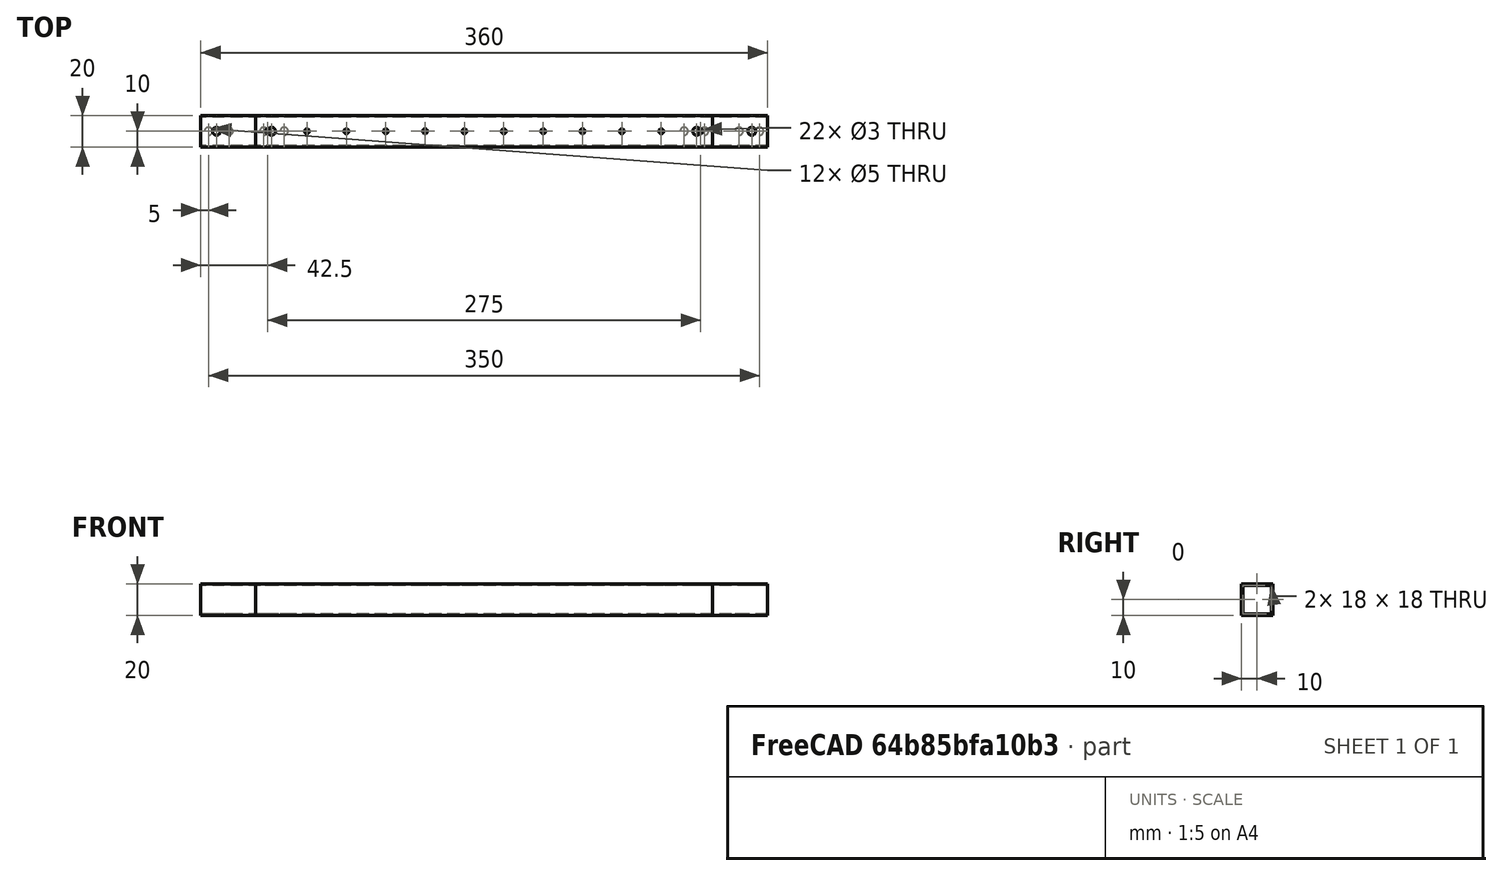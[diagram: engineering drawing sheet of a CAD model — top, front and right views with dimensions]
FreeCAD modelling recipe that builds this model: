
FCSTD DOCUMENT  (FreeCAD 0.19R24291 (Git))
Label: carbon-fiber-tube
License: Other
LicenseURL: GPL3
objects: TechDraw::DrawViewDimension×15, Sketcher::SketchObject×12, PartDesign::Pocket×10, TechDraw::DrawViewPart×6, TechDraw::DrawViewBalloon×6, PartDesign::LinearPattern×4, PartDesign::Pad×2, PartDesign::Body×2, TechDraw::DrawSVGTemplate×2, TechDraw::DrawViewAnnotation×2, TechDraw::DrawPage×2
note: 42 computed .brp shape members not serialized (recipe doc carries the construction recipe); baked Part::Feature solids carry a one-line shape summary decoded from their .brp

FEATURE [Sketcher::SketchObject] Sketch
  FullyConstrained = true
  MapMode = 5
  Support = -> [XY_Plane]
  sketch-geometry (4):
    g0: LineSegment StartX=-145 StartY=10 StartZ=0 EndX=145 EndY=10 EndZ=0
    g1: LineSegment StartX=145 StartY=10 StartZ=0 EndX=145 EndY=-10 EndZ=0
    g2: LineSegment StartX=145 StartY=-10 StartZ=0 EndX=-145 EndY=-10 EndZ=0
    g3: LineSegment StartX=-145 StartY=-10 StartZ=0 EndX=-145 EndY=10 EndZ=0
  constraints (12):
    c: Coincident(g0,g1)
    c: Coincident(g1,g2)
    c: Coincident(g2,g3)
    c: Coincident(g3,g0)
    c: Horizontal(g0)
    c: Horizontal(g2)
    c: Vertical(g1)
    c: Vertical(g3)
    c: DistanceX(g0,g0) = 290
    c: DistanceX(g0,g-1) = 145
    c: DistanceY(g3,g3) = 20
    c: DistanceY(g2,g-1) = 10
FEATURE [PartDesign::Pad] Pad
  Direction = (1,1,1)
  Length = 20
  Length2 = 100
  Profile = -> Sketch
  Type = 0
FEATURE [Sketcher::SketchObject] Sketch001
  FullyConstrained = true
  MapMode = 5
  Placement = pos=(145,0,0) rot=(0.57735,0.57735,0.57735;2.0944rad)
  Support = -> [Pad]
  sketch-geometry (4):
    g0: LineSegment StartX=-9 StartY=19 StartZ=0 EndX=9 EndY=19 EndZ=0
    g1: LineSegment StartX=9 StartY=19 StartZ=0 EndX=9 EndY=1 EndZ=0
    g2: LineSegment StartX=9 StartY=1 StartZ=0 EndX=-9 EndY=1 EndZ=0
    g3: LineSegment StartX=-9 StartY=1 StartZ=0 EndX=-9 EndY=19 EndZ=0
  constraints (12):
    c: Coincident(g0,g1)
    c: Coincident(g1,g2)
    c: Coincident(g2,g3)
    c: Coincident(g3,g0)
    c: Horizontal(g0)
    c: Horizontal(g2)
    c: Vertical(g1)
    c: Vertical(g3)
    c: DistanceX(g0,g0) = 18
    c: DistanceX(g2,g-1) = 9
    c: DistanceY(g3,g3) = 18
    c: DistanceY(g-1,g2) = 1
FEATURE [PartDesign::Pocket] Pocket
  BaseFeature = -> Pad
  Length = 5
  Length2 = 100
  Profile = -> Sketch001
  Type = 1
FEATURE [Sketcher::SketchObject] Sketch002
  FullyConstrained = true
  MapMode = 5
  Placement = pos=(0,0,20) rot=(0,0,1;0rad)
  Support = -> [Pocket]
  sketch-geometry (6):
    g0: LineSegment StartX=-145 StartY=10 StartZ=0 EndX=145 EndY=10 EndZ=0
    g1: LineSegment StartX=145 StartY=10 StartZ=0 EndX=145 EndY=-10 EndZ=0
    g2: LineSegment StartX=145 StartY=-10 StartZ=0 EndX=-145 EndY=-10 EndZ=0
    g3: LineSegment StartX=-145 StartY=-10 StartZ=0 EndX=-145 EndY=10 EndZ=0
    g4: Circle CenterX=-135 CenterY=0 CenterZ=0 NormalX=0 NormalY=0 NormalZ=1 AngleXU=0 Radius=2.5
    g5: Circle CenterX=135 CenterY=0 CenterZ=0 NormalX=0 NormalY=0 NormalZ=1 AngleXU=0 Radius=2.5
  constraints (18):
    c: Coincident(g0,g1)
    c: Coincident(g1,g2)
    c: Coincident(g2,g3)
    c: Coincident(g3,g0)
    c: Horizontal(g0)
    c: Horizontal(g2)
    c: Vertical(g1)
    c: Vertical(g3)
    c: DistanceX(g0,g0) = 290
    c: DistanceX(g0,g-1) = 145
    c: DistanceY(g3,g3) = 20
    c: DistanceY(g2,g-1) = 10
    c: PointOnObject(g4,g-1)
    c: PointOnObject(g5,g-1)
    c: Radius(g5) = 2.5
    c: Radius(g4) = 2.5
    c: DistanceX(g5,g0) = 10
    c: DistanceX(g0,g4) = 10
FEATURE [PartDesign::Pocket] Pocket001
  BaseFeature = -> Pocket
  Length = 5
  Length2 = 100
  Profile = -> Sketch002
  Type = 0
FEATURE [Sketcher::SketchObject] Sketch003
  FullyConstrained = true
  MapMode = 5
  Placement = pos=(0,0,0) rot=(1,0,0;3.14159rad)
  Support = -> [Pocket001]
  sketch-geometry (4):
    g0: Circle CenterX=-140 CenterY=0 CenterZ=0 NormalX=0 NormalY=0 NormalZ=1 AngleXU=0 Radius=2.5
    g1: Circle CenterX=-127 CenterY=0 CenterZ=0 NormalX=0 NormalY=0 NormalZ=1 AngleXU=0 Radius=2.5
    g2: Circle CenterX=140 CenterY=0 CenterZ=0 NormalX=0 NormalY=0 NormalZ=1 AngleXU=0 Radius=2.5
    g3: Circle CenterX=127 CenterY=0 CenterZ=0 NormalX=0 NormalY=0 NormalZ=1 AngleXU=0 Radius=2.5
  constraints (12):
    c: PointOnObject(g0,g-1)
    c: PointOnObject(g1,g-1)
    c: PointOnObject(g2,g-1)
    c: PointOnObject(g3,g-1)
    c: Radius(g2) = 2.5
    c: Radius(g3) = 2.5
    c: Radius(g0) = 2.5
    c: Radius(g1) = 2.5
    c: DistanceX(g0,g-1) = 140
    c: DistanceX(g1,g-1) = 127
    c: DistanceX(g-1,g2) = 140
    c: DistanceX(g-1,g3) = 127
FEATURE [PartDesign::Pocket] Pocket002
  BaseFeature = -> Pocket001
  Length = 5
  Length2 = 100
  Profile = -> Sketch003
  Type = 0
FEATURE [Sketcher::SketchObject] Sketch004
  FullyConstrained = true
  MapMode = 5
  Placement = pos=(0,0,20) rot=(0,0,1;0rad)
  Support = -> [Pocket002]
  sketch-geometry (1):
    g0: Circle CenterX=12.5 CenterY=0 CenterZ=0 NormalX=0 NormalY=0 NormalZ=1 AngleXU=0 Radius=1.5
  constraints (3):
    c: PointOnObject(g0,g-1)
    c: Radius(g0) = 1.5
    c: DistanceX(g-1,g0) = 12.5
FEATURE [PartDesign::Pocket] Pocket003
  BaseFeature = -> Pocket002
  Length = 5
  Length2 = 100
  Profile = -> Sketch004
  Type = 0
FEATURE [PartDesign::LinearPattern] LinearPattern
  BaseFeature = -> Pocket003
  Direction = -> Sketch004 [H_Axis]
  Length = 100
  Occurrences = 5
  Originals = -> [Pocket003]
FEATURE [Sketcher::SketchObject] Sketch005
  FullyConstrained = true
  MapMode = 5
  Placement = pos=(0,0,20) rot=(0,0,1;0rad)
  Support = -> [LinearPattern]
  sketch-geometry (1):
    g0: Circle CenterX=-12.5 CenterY=0 CenterZ=0 NormalX=0 NormalY=0 NormalZ=1 AngleXU=0 Radius=1.5
  constraints (3):
    c: PointOnObject(g0,g-1)
    c: Radius(g0) = 1.5
    c: DistanceX(g0,g-1) = 12.5
FEATURE [PartDesign::Pocket] Pocket004
  BaseFeature = -> LinearPattern
  Length = 5
  Length2 = 100
  Profile = -> Sketch005
  Type = 0
FEATURE [PartDesign::LinearPattern] LinearPattern001
  BaseFeature = -> Pocket004
  Direction = -> Sketch005 [H_Axis]
  Length = 100
  Occurrences = 5
  Originals = -> [Pocket004]
  Reversed = true
FEATURE [PartDesign::Body] Body  label="180-tube"
  Group = -> [Sketch,Pad,Sketch001,Pocket,Sketch002,Pocket001,Sketch003,Pocket002,Sketch004,Pocket003,LinearPattern,Sketch005,Pocket004,LinearPattern001]
  Origin = -> Origin
  Tip = -> LinearPattern001
FEATURE [Sketcher::SketchObject] Sketch006
  FullyConstrained = true
  MapMode = 5
  Support = -> [XY_Plane001]
  sketch-geometry (4):
    g0: LineSegment StartX=-180 StartY=10 StartZ=0 EndX=180 EndY=10 EndZ=0
    g1: LineSegment StartX=180 StartY=10 StartZ=0 EndX=180 EndY=-10 EndZ=0
    g2: LineSegment StartX=180 StartY=-10 StartZ=0 EndX=-180 EndY=-10 EndZ=0
    g3: LineSegment StartX=-180 StartY=-10 StartZ=0 EndX=-180 EndY=10 EndZ=0
  constraints (12):
    c: Coincident(g0,g1)
    c: Coincident(g1,g2)
    c: Coincident(g2,g3)
    c: Coincident(g3,g0)
    c: Horizontal(g0)
    c: Horizontal(g2)
    c: Vertical(g1)
    c: Vertical(g3)
    c: DistanceY(g-1,g0) = 10
    c: DistanceY(g3,g3) = 20
    c: DistanceX(g0,g0) = 360
    c: DistanceX(g0,g-1) = 180
FEATURE [PartDesign::Pad] Pad001
  Direction = (1,1,1)
  Length = 20
  Length2 = 100
  Profile = -> Sketch006
  Type = 0
FEATURE [Sketcher::SketchObject] Sketch007
  FullyConstrained = true
  MapMode = 5
  Placement = pos=(180,0,0) rot=(0.57735,0.57735,0.57735;2.0944rad)
  Support = -> [Pad001]
  sketch-geometry (4):
    g0: LineSegment StartX=-9 StartY=19 StartZ=0 EndX=9 EndY=19 EndZ=0
    g1: LineSegment StartX=9 StartY=19 StartZ=0 EndX=9 EndY=1 EndZ=0
    g2: LineSegment StartX=9 StartY=1 StartZ=0 EndX=-9 EndY=1 EndZ=0
    g3: LineSegment StartX=-9 StartY=1 StartZ=0 EndX=-9 EndY=19 EndZ=0
  constraints (12):
    c: Coincident(g0,g1)
    c: Coincident(g1,g2)
    c: Coincident(g2,g3)
    c: Coincident(g3,g0)
    c: Horizontal(g0)
    c: Horizontal(g2)
    c: Vertical(g1)
    c: Vertical(g3)
    c: DistanceX(g0,g0) = 18
    c: DistanceX(g2,g-1) = 9
    c: DistanceY(g3,g3) = 18
    c: DistanceY(g-1,g2) = 1
FEATURE [PartDesign::Pocket] Pocket005
  BaseFeature = -> Pad001
  Length = 5
  Length2 = 100
  Profile = -> Sketch007
  Type = 1
FEATURE [Sketcher::SketchObject] Sketch008
  FullyConstrained = true
  MapMode = 5
  Placement = pos=(0,0,20) rot=(0,0,1;0rad)
  Support = -> [Pocket005]
  sketch-geometry (2):
    g0: Circle CenterX=-170 CenterY=0 CenterZ=0 NormalX=0 NormalY=0 NormalZ=1 AngleXU=0 Radius=2.5
    g1: Circle CenterX=170 CenterY=0 CenterZ=0 NormalX=0 NormalY=0 NormalZ=1 AngleXU=0 Radius=2.5
  constraints (6):
    c: PointOnObject(g0,g-1)
    c: PointOnObject(g1,g-1)
    c: Radius(g1) = 2.5
    c: Radius(g0) = 2.5
    c: DistanceX(g0,g-1) = 170
    c: DistanceX(g-1,g1) = 170
FEATURE [PartDesign::Pocket] Pocket006
  BaseFeature = -> Pocket005
  Length = 5
  Length2 = 100
  Profile = -> Sketch008
  Type = 0
FEATURE [Sketcher::SketchObject] Sketch009
  FullyConstrained = true
  MapMode = 5
  Placement = pos=(0,0,0) rot=(1,0,0;3.14159rad)
  Support = -> [Pocket006]
  sketch-geometry (4):
    g0: Circle CenterX=-175 CenterY=0 CenterZ=0 NormalX=0 NormalY=0 NormalZ=1 AngleXU=0 Radius=2.5
    g1: Circle CenterX=-162 CenterY=0 CenterZ=0 NormalX=0 NormalY=0 NormalZ=1 AngleXU=0 Radius=2.5
    g2: Circle CenterX=162 CenterY=0 CenterZ=0 NormalX=0 NormalY=0 NormalZ=1 AngleXU=0 Radius=2.5
    g3: Circle CenterX=175 CenterY=0 CenterZ=0 NormalX=0 NormalY=0 NormalZ=1 AngleXU=0 Radius=2.5
  constraints (12):
    c: PointOnObject(g0,g-1)
    c: PointOnObject(g1,g-1)
    c: PointOnObject(g2,g-1)
    c: PointOnObject(g3,g-1)
    c: Radius(g0) = 2.5
    c: Radius(g1) = 2.5
    c: Radius(g2) = 2.5
    c: Radius(g3) = 2.5
    c: DistanceX(g-1,g3) = 175
    c: DistanceX(g0,g-1) = 175
    c: DistanceX(g1,g-1) = 162
    c: DistanceX(g-1,g2) = 162
FEATURE [PartDesign::Pocket] Pocket007
  BaseFeature = -> Pocket006
  Length = 5
  Length2 = 100
  Profile = -> Sketch009
  Type = 0
FEATURE [Sketcher::SketchObject] Sketch010
  FullyConstrained = true
  MapMode = 5
  Placement = pos=(0,0,20) rot=(0,0,1;0rad)
  Support = -> [Pocket007]
  sketch-geometry (1):
    g0: Circle CenterX=12.5 CenterY=0 CenterZ=0 NormalX=0 NormalY=0 NormalZ=1 AngleXU=0 Radius=1.5
  constraints (3):
    c: PointOnObject(g0,g-1)
    c: DistanceX(g-1,g0) = 12.5
    c: Radius(g0) = 1.5
FEATURE [PartDesign::Pocket] Pocket008
  BaseFeature = -> Pocket007
  Length = 5
  Length2 = 100
  Profile = -> Sketch010
  Type = 0
FEATURE [PartDesign::LinearPattern] LinearPattern002
  BaseFeature = -> Pocket008
  Direction = -> Sketch010 [H_Axis]
  Length = 125
  Occurrences = 6
  Originals = -> [Pocket008]
FEATURE [Sketcher::SketchObject] Sketch011
  FullyConstrained = true
  MapMode = 5
  Placement = pos=(0,0,20) rot=(0,0,1;0rad)
  Support = -> [LinearPattern002]
  sketch-geometry (1):
    g0: Circle CenterX=-12.5 CenterY=0 CenterZ=0 NormalX=0 NormalY=0 NormalZ=1 AngleXU=0 Radius=1.5
  constraints (3):
    c: PointOnObject(g0,g-1)
    c: Radius(g0) = 1.5
    c: DistanceX(g0,g-1) = 12.5
FEATURE [PartDesign::Pocket] Pocket009
  BaseFeature = -> LinearPattern002
  Length = 5
  Length2 = 100
  Profile = -> Sketch011
  Type = 0
FEATURE [PartDesign::LinearPattern] LinearPattern003
  BaseFeature = -> Pocket009
  Direction = -> Sketch011 [H_Axis]
  Length = 125
  Occurrences = 6
  Originals = -> [Pocket009]
  Reversed = true
FEATURE [PartDesign::Body] Body001  label="250-tube"
  Group = -> [Sketch006,Pad001,Sketch007,Pocket005,Sketch008,Pocket006,Sketch009,Pocket007,Sketch010,Pocket008,LinearPattern002,Sketch011,Pocket009,LinearPattern003]
  Origin = -> Origin001
  Tip = -> LinearPattern003
FEATURE [TechDraw::DrawSVGTemplate] Template
  EditableTexts = AuthorName=SnakeOil-XY; CheckDate=-; CreationDate=2021-12-13; DrawingNumber=1; FC-Scale=1:1; FC-Title=Carbon fiber tube; SheetNumber=1/1; Subtitle=for 180 machine; SupervisorName=SnakeOil-XY; Weight=-
  Height = 297
  Orientation = 1
  Width = 420
FEATURE [TechDraw::DrawViewPart] View  label="Top view"
  Caption = Top view
  CoarseView = false
  Direction = (0,0,1)
  Focus = 100
  HardHidden = false
  IsoCount = 0
  IsoHidden = false
  IsoVisible = false
  LockPosition = false
  Perspective = false
  Rotation = 0
  ScaleType = 0
  SeamHidden = false
  SeamVisible = true
  SmoothHidden = false
  SmoothVisible = true
  Source = -> [Body]
  X = 176.348
  XDirection = (1,0,0)
  Y = 207.934
FEATURE [TechDraw::DrawViewPart] View001  label="Bottom view"
  Caption = Bottom view
  CoarseView = false
  Direction = (0,0,-1)
  Focus = 100
  HardHidden = false
  IsoCount = 0
  IsoHidden = false
  IsoVisible = false
  LockPosition = false
  Perspective = false
  Rotation = 0
  ScaleType = 0
  SeamHidden = false
  SeamVisible = true
  SmoothHidden = false
  SmoothVisible = true
  Source = -> [Body]
  X = 176.869
  XDirection = (1,0,0)
  Y = 136.232
FEATURE [TechDraw::DrawViewPart] View002  label="Side view"
  Caption = Side view
  CoarseView = false
  Direction = (1,0,0)
  Focus = 100
  HardHidden = false
  IsoCount = 0
  IsoHidden = false
  IsoVisible = false
  LockPosition = false
  Perspective = false
  Rotation = 0
  ScaleType = 0
  SeamHidden = false
  SeamVisible = true
  SmoothHidden = false
  SmoothVisible = true
  Source = -> [Body]
  X = 374.249
  XDirection = (0,1,0)
  Y = 209.472
FEATURE [TechDraw::DrawViewDimension] Dimension
  Arbitrary = false
  ArbitraryTolerances = false
  EqualTolerance = true
  FormatSpec = %.2f
  FormatSpecOverTolerance = %+.2f
  FormatSpecUnderTolerance = %+.2f
  Inverted = false
  LockPosition = false
  MeasureType = 1
  OverTolerance = 0
  References2D = -> [View]
  Rotation = 0
  ScaleType = 0
  TheoreticalExact = false
  Type = 1
  UnderTolerance = 0
  X = -138.865
  Y = 21.8119
FEATURE [TechDraw::DrawViewDimension] Dimension001
  Arbitrary = false
  ArbitraryTolerances = false
  EqualTolerance = true
  FormatSpec = %.2f
  FormatSpecOverTolerance = %+.2f
  FormatSpecUnderTolerance = %+.2f
  Inverted = false
  LockPosition = false
  MeasureType = 1
  OverTolerance = 0
  References2D = -> [View001]
  Rotation = 0
  ScaleType = 0
  TheoreticalExact = false
  Type = 1
  UnderTolerance = 0
  X = -152.885
  Y = 23.261
FEATURE [TechDraw::DrawViewDimension] Dimension002
  Arbitrary = false
  ArbitraryTolerances = false
  EqualTolerance = true
  FormatSpec = %.2f
  FormatSpecOverTolerance = %+.2f
  FormatSpecUnderTolerance = %+.2f
  Inverted = false
  LockPosition = false
  MeasureType = 1
  OverTolerance = 0
  References2D = -> [View001]
  Rotation = 0
  ScaleType = 0
  TheoreticalExact = false
  Type = 1
  UnderTolerance = 0
  X = -133.84
  Y = 23.3238
FEATURE [TechDraw::DrawViewAnnotation] Annotation
  Font = osifont
  LineSpace = 80
  LockPosition = false
  MaxWidth = -1
  Rotation = 0
  ScaleType = 0
  Text = Dimensions in mm
  TextSize = 5
  TextStyle = 0
  X = 286.959
  Y = 32.355
FEATURE [TechDraw::DrawViewDimension] Dimension003
  Arbitrary = false
  ArbitraryTolerances = false
  EqualTolerance = true
  FormatSpec = %.2f
  FormatSpecOverTolerance = %+.2f
  FormatSpecUnderTolerance = %+.2f
  Inverted = false
  LockPosition = false
  MeasureType = 1
  OverTolerance = 0
  References2D = -> [View]
  Rotation = 0
  ScaleType = 0
  TheoreticalExact = false
  Type = 1
  UnderTolerance = 0
  X = -124.164
  Y = 21.8129
FEATURE [TechDraw::DrawViewDimension] Dimension004
  Arbitrary = false
  ArbitraryTolerances = false
  EqualTolerance = true
  FormatSpec = %.2f
  FormatSpecOverTolerance = %+.2f
  FormatSpecUnderTolerance = %+.2f
  Inverted = false
  LockPosition = false
  MeasureType = 1
  OverTolerance = 0
  References2D = -> [View]
  Rotation = 0
  ScaleType = 0
  TheoreticalExact = false
  Type = 1
  UnderTolerance = 0
  X = -100.118
  Y = 21.8129
FEATURE [TechDraw::DrawViewBalloon] Balloon001
  BubbleShape = 1
  EndType = 0
  EndTypeScale = 1
  KinkLength = 5
  LockPosition = false
  OriginX = 134.46
  OriginY = -0.397655
  Rotation = 0
  ScaleType = 0
  ShapeScale = 1
  SourceView = -> View
  Text = 2x M5
  TextWrapLen = -1
  X = 156.086
  Y = -21.4953
FEATURE [TechDraw::DrawViewDimension] Dimension005
  Arbitrary = false
  ArbitraryTolerances = false
  EqualTolerance = true
  FormatSpec = %.2f
  FormatSpecOverTolerance = %+.2f
  FormatSpecUnderTolerance = %+.2f
  Inverted = false
  LockPosition = false
  MeasureType = 1
  OverTolerance = 0
  References2D = -> [View]
  Rotation = 0
  ScaleType = 0
  TheoreticalExact = false
  Type = 1
  UnderTolerance = 0
  X = -6.38086
  Y = 32.043
FEATURE [TechDraw::DrawViewBalloon] Balloon
  BubbleShape = 1
  EndType = 0
  EndTypeScale = 1
  KinkLength = 5
  LockPosition = false
  OriginX = 112.052
  OriginY = -0.387355
  Rotation = 0
  ScaleType = 0
  ShapeScale = 1
  SourceView = -> View
  Text = 10x M3
  TextWrapLen = -1
  X = 140.78
  Y = 34.6517
FEATURE [TechDraw::DrawViewDimension] Dimension006
  Arbitrary = false
  ArbitraryTolerances = false
  EqualTolerance = true
  FormatSpec = %.2f
  FormatSpecOverTolerance = %+.2f
  FormatSpecUnderTolerance = %+.2f
  Inverted = false
  LockPosition = false
  MeasureType = 1
  OverTolerance = 0
  References2D = -> [View]
  Rotation = 0
  ScaleType = 0
  TheoreticalExact = false
  Type = 2
  UnderTolerance = 0
  X = 150.618
  Y = 1.94082
FEATURE [TechDraw::DrawSVGTemplate] Template001
  EditableTexts = AuthorName=SnakeOil-XY; CheckDate=-; CreationDate=2021-12-13; DrawingNumber=1; FC-Scale=1:1; FC-Title=Carbon fiber tube; SheetNumber=1/1; Subtitle=for 250 machine; SupervisorName=SnakeOil-XY; Weight=-
  Height = 297
  Orientation = 1
  Width = 420
FEATURE [TechDraw::DrawViewPart] View003  label="Top view001"
  Caption = Top view
  CoarseView = false
  Direction = (0,0,1)
  Focus = 100
  HardHidden = false
  IsoCount = 0
  IsoHidden = false
  IsoVisible = false
  LockPosition = false
  Perspective = false
  Rotation = 0
  ScaleType = 0
  SeamHidden = false
  SeamVisible = true
  SmoothHidden = false
  SmoothVisible = true
  Source = -> [Body001]
  X = 205.876
  XDirection = (1,0,0)
  Y = 235.646
FEATURE [TechDraw::DrawViewPart] View004  label="Bottom view001"
  Caption = Bottom view
  CoarseView = false
  Direction = (0,0,-1)
  Focus = 100
  HardHidden = false
  IsoCount = 0
  IsoHidden = false
  IsoVisible = false
  LockPosition = false
  Perspective = false
  Rotation = 0
  ScaleType = 0
  SeamHidden = false
  SeamVisible = true
  SmoothHidden = false
  SmoothVisible = true
  Source = -> [Body001]
  X = 206.538
  XDirection = (1,0,0)
  Y = 175.811
FEATURE [TechDraw::DrawViewPart] View005  label="Side view001"
  Caption = Side view
  CoarseView = false
  Direction = (1,0,0)
  Focus = 100
  HardHidden = false
  IsoCount = 0
  IsoHidden = false
  IsoVisible = false
  LockPosition = false
  Perspective = false
  Rotation = 0
  ScaleType = 0
  SeamHidden = false
  SeamVisible = true
  SmoothHidden = false
  SmoothVisible = true
  Source = -> [Body001]
  X = 370.47
  XDirection = (0,1,0)
  Y = 112.486
FEATURE [TechDraw::DrawViewAnnotation] Annotation001
  Font = osifont
  LineSpace = 80
  LockPosition = false
  MaxWidth = -1
  Rotation = 0
  ScaleType = 0
  Text = Dimensions in mm
  TextSize = 5
  TextStyle = 0
  X = 287.894
  Y = 31.9482
FEATURE [TechDraw::DrawViewDimension] Dimension007
  Arbitrary = false
  ArbitraryTolerances = false
  EqualTolerance = true
  FormatSpec = %.2f
  FormatSpecOverTolerance = %+.2f
  FormatSpecUnderTolerance = %+.2f
  Inverted = false
  LockPosition = false
  MeasureType = 1
  OverTolerance = 0
  References2D = -> [View005]
  Rotation = 0
  ScaleType = 0
  TheoreticalExact = false
  Type = 2
  UnderTolerance = 0
  X = 14.8695
  Y = 2.08691
FEATURE [TechDraw::DrawViewDimension] Dimension008
  Arbitrary = false
  ArbitraryTolerances = false
  EqualTolerance = true
  FormatSpec = %.2f
  FormatSpecOverTolerance = %+.2f
  FormatSpecUnderTolerance = %+.2f
  Inverted = false
  LockPosition = false
  MeasureType = 1
  OverTolerance = 0
  References2D = -> [View002]
  Rotation = 0
  ScaleType = 0
  TheoreticalExact = false
  Type = 2
  UnderTolerance = 0
  X = 14.1676
  Y = 1.47094
FEATURE [TechDraw::DrawViewDimension] Dimension009
  Arbitrary = false
  ArbitraryTolerances = false
  EqualTolerance = true
  FormatSpec = %.2f
  FormatSpecOverTolerance = %+.2f
  FormatSpecUnderTolerance = %+.2f
  Inverted = false
  LockPosition = false
  MeasureType = 1
  OverTolerance = 0
  References2D = -> [View003]
  Rotation = 0
  ScaleType = 0
  TheoreticalExact = false
  Type = 1
  UnderTolerance = 0
  X = -0.812835
  Y = 33.1658
FEATURE [TechDraw::DrawViewDimension] Dimension010
  Arbitrary = false
  ArbitraryTolerances = false
  EqualTolerance = true
  FormatSpec = %.2f
  FormatSpecOverTolerance = %+.2f
  FormatSpecUnderTolerance = %+.2f
  Inverted = false
  LockPosition = false
  MeasureType = 1
  OverTolerance = 0
  References2D = -> [View003]
  Rotation = 0
  ScaleType = 0
  TheoreticalExact = false
  Type = 1
  UnderTolerance = 0
  X = -175.102
  Y = 21.1551
FEATURE [TechDraw::DrawViewDimension] Dimension011
  Arbitrary = false
  ArbitraryTolerances = false
  EqualTolerance = true
  FormatSpec = %.2f
  FormatSpecOverTolerance = %+.2f
  FormatSpecUnderTolerance = %+.2f
  Inverted = false
  LockPosition = false
  MeasureType = 1
  OverTolerance = 0
  References2D = -> [View003]
  Rotation = 0
  ScaleType = 0
  TheoreticalExact = false
  Type = 1
  UnderTolerance = 0
  X = -154.766
  Y = 21.1337
FEATURE [TechDraw::DrawViewDimension] Dimension012
  Arbitrary = false
  ArbitraryTolerances = false
  EqualTolerance = true
  FormatSpec = %.2f
  FormatSpecOverTolerance = %+.2f
  FormatSpecUnderTolerance = %+.2f
  Inverted = false
  LockPosition = false
  MeasureType = 1
  OverTolerance = 0
  References2D = -> [View003]
  Rotation = 0
  ScaleType = 0
  TheoreticalExact = false
  Type = 1
  UnderTolerance = 0
  X = -124.39
  Y = 21.1337
FEATURE [TechDraw::DrawViewDimension] Dimension013
  Arbitrary = false
  ArbitraryTolerances = false
  EqualTolerance = true
  FormatSpec = %.2f
  FormatSpecOverTolerance = %+.2f
  FormatSpecUnderTolerance = %+.2f
  Inverted = false
  LockPosition = false
  MeasureType = 1
  OverTolerance = 0
  References2D = -> [View004]
  Rotation = 0
  ScaleType = 0
  TheoreticalExact = false
  Type = 1
  UnderTolerance = 0
  X = -190.372
  Y = 24.8716
FEATURE [TechDraw::DrawViewDimension] Dimension014
  Arbitrary = false
  ArbitraryTolerances = false
  EqualTolerance = true
  FormatSpec = %.2f
  FormatSpecOverTolerance = %+.2f
  FormatSpecUnderTolerance = %+.2f
  Inverted = false
  LockPosition = false
  MeasureType = 1
  OverTolerance = 0
  References2D = -> [View004]
  Rotation = 0
  ScaleType = 0
  TheoreticalExact = false
  Type = 1
  UnderTolerance = 0
  X = -168.839
  Y = 24.8084
FEATURE [TechDraw::DrawViewBalloon] Balloon003
  BubbleShape = 1
  EndType = 0
  EndTypeScale = 1
  KinkLength = 5
  LockPosition = false
  OriginX = 169.245
  OriginY = -0.600012
  Rotation = 0
  ScaleType = 0
  ShapeScale = 1
  SourceView = -> View003
  Text = 2x M5
  TextWrapLen = -1
  X = 192.213
  Y = -14.4544
FEATURE [TechDraw::DrawViewBalloon] Balloon004
  BubbleShape = 1
  EndType = 0
  EndTypeScale = 1
  KinkLength = 5
  LockPosition = false
  OriginX = 137.338
  OriginY = -0.043502
  Rotation = 0
  ScaleType = 0
  ShapeScale = 1
  SourceView = -> View003
  Text = 12x M3
  TextWrapLen = -1
  X = 157.431
  Y = 19.9565
FEATURE [TechDraw::DrawViewBalloon] Balloon005
  BubbleShape = 1
  EndType = 0
  EndTypeScale = 1
  KinkLength = 5
  LockPosition = false
  OriginX = 175.075
  OriginY = -0.404367
  Rotation = 0
  ScaleType = 0
  ShapeScale = 1
  SourceView = -> View004
  Text = 4x M5
  TextWrapLen = -1
  X = 193.406
  Y = 15.6073
FEATURE [TechDraw::DrawPage] Page001  label="250-tube-drawing"
  KeepUpdated = true
  NextBalloonIndex = 4
  ProjectionType = 0
  Template = -> Template001
  Views = -> [View003,View004,View005,Annotation001,Dimension007,Dimension009,Dimension010,Dimension011,Dimension012,Dimension013,Dimension014,Balloon003,Balloon004,Balloon005]
FEATURE [TechDraw::DrawViewBalloon] Balloon006
  BubbleShape = 1
  EndType = 0
  EndTypeScale = 1
  KinkLength = 5
  LockPosition = false
  OriginX = 139.705
  OriginY = -0.701373
  Rotation = 0
  ScaleType = 0
  ShapeScale = 1
  SourceView = -> View001
  Text = 4x M5
  TextWrapLen = -1
  X = 161.252
  Y = -16.8596
FEATURE [TechDraw::DrawPage] Page  label="180-tube-drawing"
  KeepUpdated = true
  NextBalloonIndex = 6
  ProjectionType = 0
  Template = -> Template
  Views = -> [View,View001,View002,Dimension,Dimension001,Dimension002,Annotation,Dimension003,Dimension004,Balloon001,Dimension005,Balloon,Dimension006,Dimension008,Balloon006]
